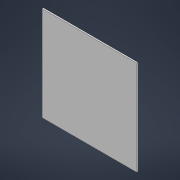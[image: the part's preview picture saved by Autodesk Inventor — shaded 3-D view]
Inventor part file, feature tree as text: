
AUTODESK INVENTOR PART (.ipt)
format: ipt  version: 2022 (Build 260153000, 153)  size: 83,968 bytes
history: native  units: mm
features: extrude x1, sketch x1
ambient origin geometry x8: Origin, YZ Plane, XZ Plane, XY Plane, X Axis, Y Axis, Z Axis, Center Point
bodies: Solid1 (feature_tree)
feature tree (2):
  extrude  "Extrusion1"  Depth=216.0mm
  sketch  "Sketch1"  dims[d0=216.0mm d1=216.0mm d2=3.0mm d3=0.0mm]
